# Revit family: ALSPEC ThermAFrame® 101.6&150  Flush CT GLZ Thermally Broken
name_source: partatom
category: Curtain Panels
revit_build: Autodesk Revit 2017 (Build: 20160225_1515(x64)
units: mm (PartAtom-declared; Revit-internal decimal feet)

## family parameters
Always vertical = Yes
Cut with Voids When Loaded = No
OmniClass Number = 23.25.20.14.11.11.17
OmniClass Title = Infill Panels
Shared = No

## types (1)
- ALSPEC ThermAFrame® 101.6  Flush GLZ Thermally Broken
    A = 8 mm  [stored 0.0262467 ft]
    ANZRC Compliant = Yes
    Analytic Construction = <None>
    B = 20 mm  [stored 0.0656168 ft]
    C = 20 mm  [stored 0.0656168 ft]
    D = 4 mm  [stored 0.0131234 ft]
    DOUBLE GLAZED THICKNESS = 20 mm  [stored 0.0656168 ft]
    SINGLE GLAZED THICKNESS = 8 mm  [stored 0.0262467 ft]
    TODAYS DATE = 05.02.2019
    VERSION = 2.0
    YEAR = 2019

note: [stored X ft] marks values corroborated as IEEE doubles in the binary element streams (Revit-internal decimal feet)

## geometry (parser evidence)
native form markers: Sweep x3
no freeform markers — native parametric forms only
